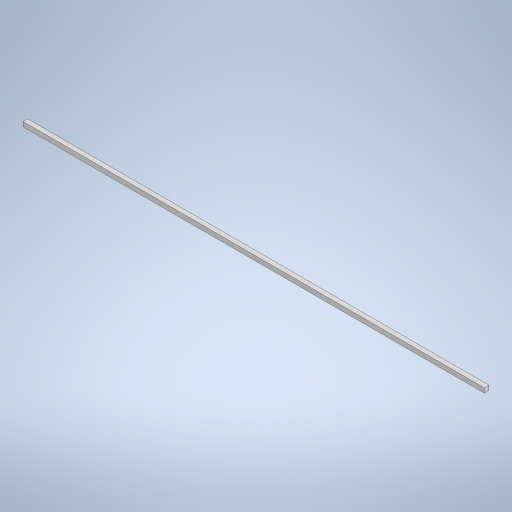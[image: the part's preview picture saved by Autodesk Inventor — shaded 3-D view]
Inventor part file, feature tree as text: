
AUTODESK INVENTOR PART (.ipt)
format: ipt  version: 2024 (Build 280153000, 153)  size: 247,808 bytes
history: native  units: in
note: dims shown in document units (in); Inventor stores cm internally (conversion verified against a paired STEP export)
features: extrude x2, sketch x2, projected_geometry x1
ambient origin geometry x8: Origin, YZ Plane, XZ Plane, XY Plane, X Axis, Y Axis, Z Axis, Center Point
bodies: Solid1 (feature_tree)
feature tree (5):
  extrude  "Extrusion1"  Depth=0.3937in TaperAngle=0.0deg
  extrude  "Extrusion2"  [1 undecoded]
  sketch  "Sketch2"  dims[d5=0.3937in d6=0.0in d7=7.874in d8=0.0in]
  sketch  "Sketch3"
  projected_geometry  "Projected Loop1"
note: 1 required parameter value undecoded (feature->parameter linkage not recoverable at this tier; creation-order binding heuristic only, values carry confidence <= 0.55)
